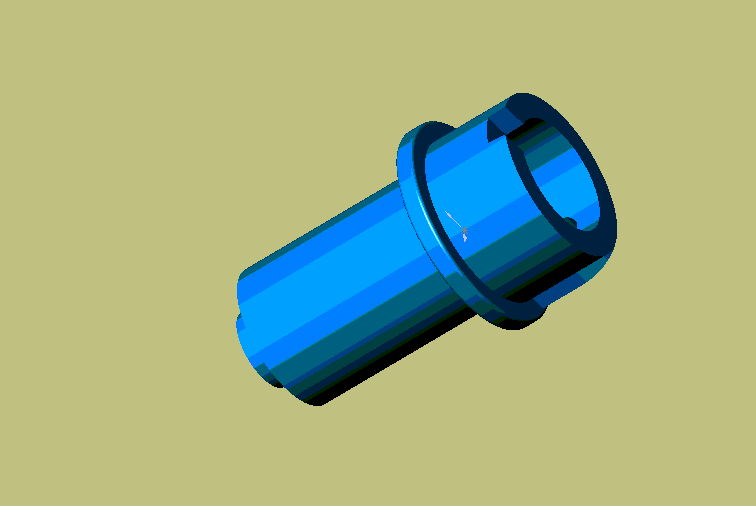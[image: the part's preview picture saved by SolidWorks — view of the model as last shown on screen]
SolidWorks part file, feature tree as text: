
SOLIDWORKS PART (.sldprt)
format: sldprt  version: not decoded by parser v0  size: 211,456 bytes
history: native  units: mm
features: sketch x9, extrude x5, plane x4, cut_extrude x4, material x1, fillet x1 (+8 scaffold rows collapsed)
feature tree (32):
  scaffold x8  (default folders/planes/origin — collapsed)
  material  "Matériau <non spécifié>"
  plane  "Plane1"
  plane  "Plane2"
  plane  "Plane3"
  sketch  "Esquisse1"  dims[D1=11.0mm]
  extrude  "Base-Extrusion"  Depth=16mm
  sketch  "Esquisse2"  dims[D1=6.0mm]
  extrude  "Boss.-Extru.1"  Depth=2mm
  sketch  "Esquisse3"  dims[D1=16.0mm]
  extrude  "Boss.-Extru.2"  Depth=1.5mm
  sketch  "Esquisse4"  dims[D1=13.0mm]
  extrude  "Boss.-Extru.3"  Depth=7mm
  sketch  "Esquisse5"  dims[D1=9.0mm]
  cut_extrude  "Enlèv. mat.-Extru.1"  Depth=19mm
  sketch  "Esquisse6"  dims[D1=3.0mm]
  cut_extrude  "Enlèv. mat.-Extru.2"  Depth=1.5mm
  plane  "Plan1"  Offset=5mm
  sketch  "Esquisse7"  dims[D2=6.0mm D1=3.5mm]
  extrude  "Boss.-Extru.4"  Depth=2mm
  sketch  "Esquisse8"  dims[D1=3.0mm]
  cut_extrude  "Enlèv. mat.-Extru.3"  [1 undecoded]
  sketch  "Esquisse9"  dims[D1=3.0mm]
  cut_extrude  "Enlèv. mat.-Extru.4"  [1 undecoded]
  fillet  "Congé2"  Radius=0.25mm
decode coverage: 17 of 19 modeling features carry decoded parameters
note: 2 parameter values undecoded
note: suppression state not decoded; provenance and decode notes live in map.json
